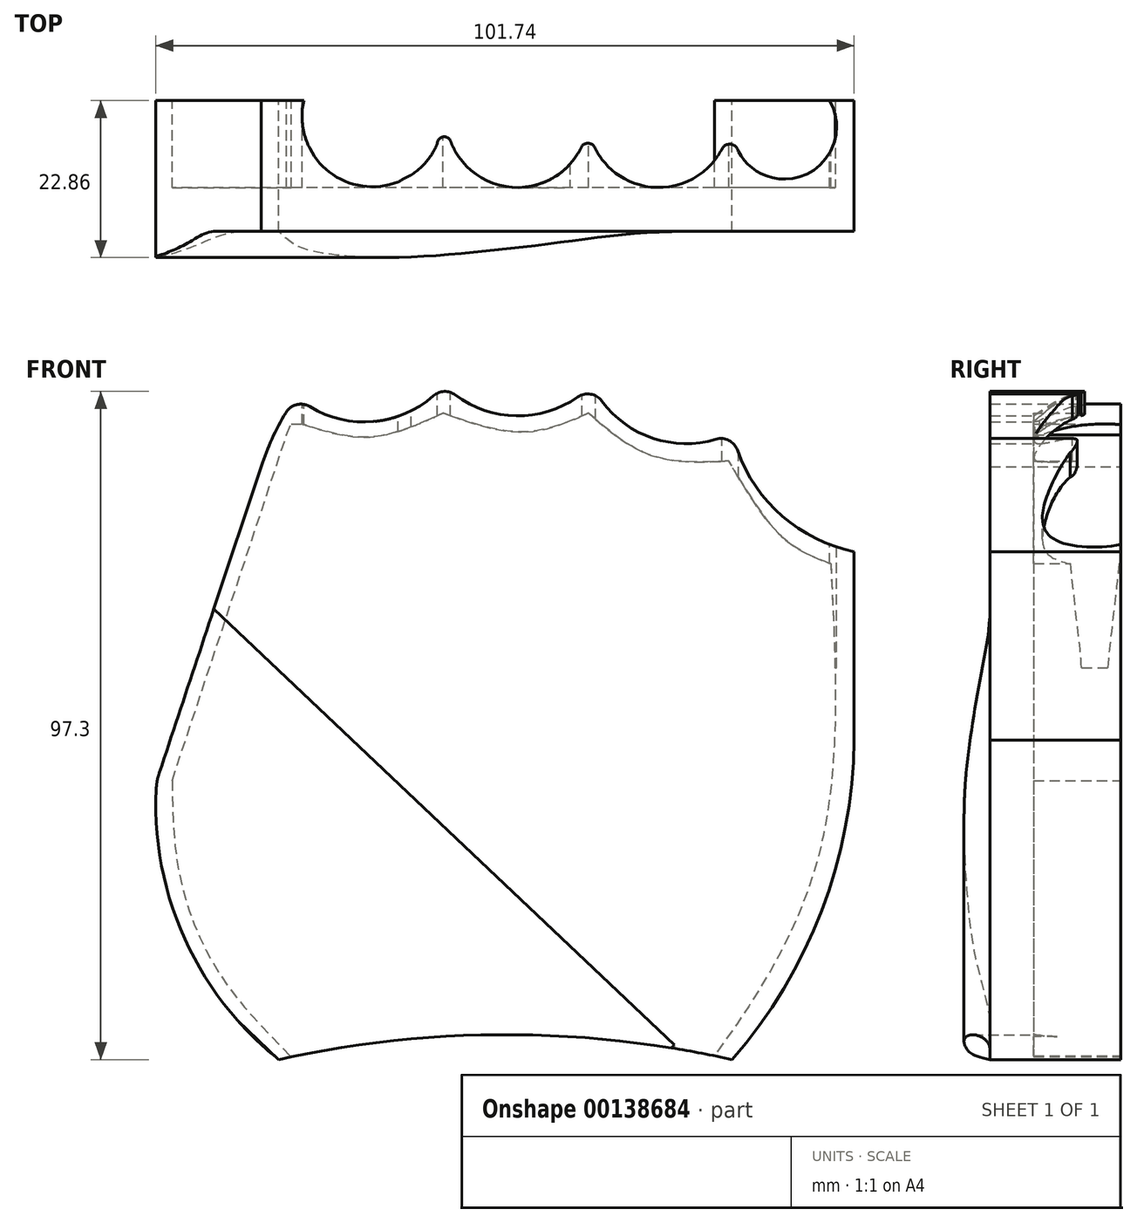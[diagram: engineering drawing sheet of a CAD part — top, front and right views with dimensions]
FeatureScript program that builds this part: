
annotation { "Feature Type Name" : "Feature", "Feature Type Description" : "" }
export const myFeature = defineFeature(function(context is Context, id is Id, definition is map)
    precondition{}
    {
        {
            var Q0;
            Q0=qCreatedBy(makeId("Front.planeOp"),FACE);
            var sketch = newSketch(context, id + "F0", { "sketchPlane" : qUnion([Q0])});
            skLineSegment(sketch, "E0", {"start": v(-118.33, 125.83) * mm, "end": v(-118.33, -51.97) * mm});
            skLineSegment(sketch, "E1", {"start": v(-118.33, -51.97) * mm, "end": v(59.47, -51.97) * mm});
            skPoint(sketch, "E2", {"position": v(-59.61, -44.35) * mm});
            skPoint(sketch, "E3", {"position": v(6.43, -44.35) * mm});
            skArc(sketch, "E4", {"start": v(6.43, -44.35) * mm, "mid": v(-26.6, -40.73) * mm, "end": v(-59.61, -44.35) * mm});
            skArc(sketch, "E5", {"start": v(6.43, -44.35) * mm, "mid": v(19.48, -22.66) * mm, "end": v(24.2, 2.2) * mm});
            skLineSegment(sketch, "E6", {"start": v(-77.4, -3.7) * mm, "end": v(47.54, -3.7) * mm});
            skArc(sketch, "E7", {"start": v(-77.47, -5) * mm, "mid": v(-73.3, -26.82) * mm, "end": v(-59.61, -44.35) * mm});
            skLineSegment(sketch, "E8", {"start": v(-77.03, -2.6) * mm, "end": v(-62.15, 42.01) * mm});
            skLineSegment(sketch, "E9", {"start": v(-57.07, 52.17) * mm, "end": v(-35.55, 53.88) * mm});
            skLineSegment(sketch, "E10", {"start": v(-35.55, 53.88) * mm, "end": v(-13.96, 53.88) * mm});
            skLineSegment(sketch, "E11", {"start": v(24.2, 2.2) * mm, "end": v(24.2, 29.63) * mm});
            skCircle(sketch, "E12", {"center": v(-21.51, -1.17) * mm, "radius": 22.35 * mm});
            skCircle(sketch, "E13", {"center": v(-21.51, -1.17) * mm, "radius": 15.75 * mm});
            skArc(sketch, "E14", {"start": v(-55.08, 50.73) * mm, "mid": v(-45.83, 48.57) * mm, "end": v(-37.1, 52.31) * mm});
            skArc(sketch, "E15", {"start": v(-33.9, 52.44) * mm, "mid": v(-25.02, 49.4) * mm, "end": v(-16.05, 52.13) * mm});
            skArc(sketch, "E16", {"start": v(24.2, 2.2) * mm, "mid": v(24.87, 15.91) * mm, "end": v(24.2, 29.63) * mm});
            skArc(sketch, "E17", {"start": v(-58.58, 49.87) * mm, "mid": v(-60.6, 46.05) * mm, "end": v(-62.15, 42.01) * mm});
            skLineSegment(sketch, "E18", {"start": v(-13.96, 53.88) * mm, "end": v(6.48, 46.93) * mm});
            skLineSegment(sketch, "E19", {"start": v(6.48, 46.93) * mm, "end": v(24.2, 29.63) * mm});
            skArc(sketch, "E20", {"start": v(-12.55, 51.55) * mm, "mid": v(-5.11, 46.14) * mm, "end": v(4.09, 45.99) * mm});
            skArc(sketch, "E21", {"start": v(7.21, 44.4) * mm, "mid": v(13.76, 34.78) * mm, "end": v(24.2, 29.63) * mm});
            skPoint(sketch, "E22.visualSharp", {"position": v(-62.15, 19.11) * mm});
            skPoint(sketch, "E23.visualSharp", {"position": v(-77.4, -3.7) * mm});
            skArc(sketch, "E23.filletArc", {"start": v(-77.03, -2.6) * mm, "mid": v(-77.33, -3.78) * mm, "end": v(-77.47, -5) * mm});
            skLineSegment(sketch, "E24.bottom", {"start": v(-118.33, 125.83) * mm, "end": v(-123.4, 125.83) * mm});
            skLineSegment(sketch, "E24.top", {"start": v(-118.33, -51.97) * mm, "end": v(-123.4, -51.97) * mm});
            skLineSegment(sketch, "E24.right", {"start": v(-123.4, 125.83) * mm, "end": v(-123.4, -51.97) * mm});
            skLineSegment(sketch, "E25.bottom", {"start": v(59.47, -51.97) * mm, "end": v(-123.4, -51.97) * mm});
            skLineSegment(sketch, "E25.top", {"start": v(59.47, -57.05) * mm, "end": v(-123.4, -57.05) * mm});
            skLineSegment(sketch, "E25.left", {"start": v(59.47, -51.97) * mm, "end": v(59.47, -57.05) * mm});
            skLineSegment(sketch, "E25.right", {"start": v(-123.4, -51.97) * mm, "end": v(-123.4, -57.05) * mm});
            skPoint(sketch, "E26.visualSharp", {"position": v(-57.07, 52.17) * mm});
            skArc(sketch, "E26.filletArc", {"start": v(-55.08, 50.73) * mm, "mid": v(-57, 51.03) * mm, "end": v(-58.58, 49.87) * mm});
            skPoint(sketch, "E27.visualSharp", {"position": v(-35.55, 53.88) * mm});
            skArc(sketch, "E27.filletArc", {"start": v(-33.9, 52.44) * mm, "mid": v(-35.51, 52.95) * mm, "end": v(-37.1, 52.31) * mm});
            skPoint(sketch, "E28.visualSharp", {"position": v(-13.96, 53.88) * mm});
            skArc(sketch, "E28.filletArc", {"start": v(-12.55, 51.55) * mm, "mid": v(-14.18, 52.55) * mm, "end": v(-16.05, 52.13) * mm});
            skPoint(sketch, "E29.visualSharp", {"position": v(6.48, 46.93) * mm});
            skArc(sketch, "E29.filletArc", {"start": v(7.21, 44.4) * mm, "mid": v(5.97, 45.82) * mm, "end": v(4.09, 45.99) * mm});
            skFitSpline(sketch, "E30", {"points": [v(-58.58, 49.87) * mm, v(-64.47, 22.99) * mm, v(-69.79, 19.11) * mm], "startDerivative": vector(-6.28, -49.5) * mm, "endDerivative": vector(-17.41, -7.17) * mm});
            skSolve(sketch);
        }
        {
            var Q0;
            {var subQ4=sQuery(id+"F0.wireOp",EDGE,"E11");Q0=makeQuery(id+"F0.imprint","IMPRINT",FACE,{"disambiguationData":[TD([[makeQuery(id+"F0.imprint","IMPRINT",EDGE,{"derivedFrom":subQ4}),1.0]])]});}
            var Q1;
            {var subQ7=sQuery(id+"F0.wireOp",EDGE,"E4");Q1=makeQuery(id+"F0.imprint","IMPRINT",FACE,{"disambiguationData":[TD([[makeQuery(id+"F0.imprint","IMPRINT",EDGE,{"derivedFrom":subQ7}),-1.0]])]});}
            var Q2;
            {var subQ0=sQuery(id+"F0.wireOp",EDGE,"E13");var subQ1=sQuery(id+"F0.wireOp",EDGE,"E6");var subQ2=makeQuery(id+"F0.imprint","INTERSECT",VERTEX,{"disambiguationData":[OD(0.0)],"derivedFrom":[subQ1,subQ0]});Q2=makeQuery(id+"F0.imprint","IMPRINT",FACE,{"disambiguationData":[TD([[makeQuery(id+"F0.imprint","IMPRINT",EDGE,{"disambiguationData":[TD([[subQ2,-1.0]])],"derivedFrom":subQ1}),1.0]])]});}
            var Q3;
            {var subQ4=sQuery(id+"F0.wireOp",EDGE,"E8");Q3=makeQuery(id+"F0.imprint","IMPRINT",FACE,{"disambiguationData":[TD([[makeQuery(id+"F0.imprint","IMPRINT",EDGE,{"derivedFrom":subQ4}),-1.0]])]});}
            var Q4;
            {var subQ0=sQuery(id+"F0.wireOp",EDGE,"E13");var subQ1=sQuery(id+"F0.wireOp",EDGE,"E6");var subQ2=makeQuery(id+"F0.imprint","INTERSECT",VERTEX,{"disambiguationData":[OD(0.0)],"derivedFrom":[subQ1,subQ0]});Q4=makeQuery(id+"F0.imprint","IMPRINT",FACE,{"disambiguationData":[TD([[makeQuery(id+"F0.imprint","IMPRINT",EDGE,{"disambiguationData":[TD([[subQ2,-1.0]])],"derivedFrom":subQ1}),-1.0]])]});}
            var Q5;
            {var subQ0=sQuery(id+"F0.wireOp",EDGE,"E12");var subQ1=sQuery(id+"F0.wireOp",EDGE,"E6");var subQ2=makeQuery(id+"F0.imprint","INTERSECT",VERTEX,{"disambiguationData":[OD(0.0)],"derivedFrom":[subQ1,subQ0]});Q5=makeQuery(id+"F0.imprint","IMPRINT",FACE,{"disambiguationData":[TD([[makeQuery(id+"F0.imprint","IMPRINT",EDGE,{"disambiguationData":[TD([[subQ2,-1.0]])],"derivedFrom":subQ1}),1.0]])]});}
            var Q6;
            {var subQ0=sQuery(id+"F0.wireOp",EDGE,"E12");var subQ1=sQuery(id+"F0.wireOp",EDGE,"E6");var subQ2=makeQuery(id+"F0.imprint","INTERSECT",VERTEX,{"disambiguationData":[OD(0.0)],"derivedFrom":[subQ1,subQ0]});Q6=makeQuery(id+"F0.imprint","IMPRINT",FACE,{"disambiguationData":[TD([[makeQuery(id+"F0.imprint","IMPRINT",EDGE,{"disambiguationData":[TD([[subQ2,-1.0]])],"derivedFrom":subQ1}),-1.0]])]});}
            extrude(context, id + "F1", {"entities" : qUnion([Q0, Q1, Q2, Q3, Q4, Q5, Q6]), "depth" : 13.97 * mm});
        }
        {
            var Q0;
            Q0=qCreatedBy(makeId("Top.planeOp"),FACE);
            cPlane(context, id + "F2", {"entities" : qUnion([Q0]), "cplaneType" : CPlaneType.OFFSET, "offset" : 63.5 * mm, "width" : 152.4 * mm, "height" : 152.4 * mm});
        }
        {
            var Q0;
            Q0=qCreatedBy(id+"F2.planeOp",FACE);
            var sketch = newSketch(context, id + "F3", { "sketchPlane" : qUnion([Q0])});
            skLineSegment(sketch, "E31.0.0", {"start": v(-77.47, 0) * mm, "end": v(-77.47, 0) * mm});
            skLineSegment(sketch, "E31.0.1", {"start": v(-77.47, 0) * mm, "end": v(-77.47, -13.97) * mm});
            skLineSegment(sketch, "E31.0.2", {"start": v(-77.47, -13.97) * mm, "end": v(-77.47, -13.97) * mm});
            skLineSegment(sketch, "E31.0.3", {"start": v(-77.47, 0) * mm, "end": v(-77.47, -13.97) * mm});
            skLineSegment(sketch, "E32.0", {"start": v(24.2, -13.97) * mm, "end": v(24.2, 0) * mm});
            skLineSegment(sketch, "E33.0", {"start": v(7.21, -13.97) * mm, "end": v(24.2, -13.97) * mm});
            skLineSegment(sketch, "E34.0", {"start": v(-12.55, -13.97) * mm, "end": v(4.09, -13.97) * mm});
            skCircle(sketch, "E35", {"center": v(14.05, -3.81) * mm, "radius": 7.62 * mm});
            skCircle(sketch, "E36", {"center": v(-4.27, -2.29) * mm, "radius": 10.37 * mm});
            skCircle(sketch, "E37", {"center": v(-45.97, -2.29) * mm, "radius": 10.26 * mm});
            skCircle(sketch, "E38", {"center": v(-24.86, -2.29) * mm, "radius": 10.37 * mm});
            skArc(sketch, "E39", {"start": v(-34.62, -5.8) * mm, "mid": v(-35.78, -5.3) * mm, "end": v(-36.53, -6.3) * mm});
            skArc(sketch, "E40", {"start": v(-13.46, -7.09) * mm, "mid": v(-14.28, -6.26) * mm, "end": v(-15.4, -6.55) * mm});
            skArc(sketch, "E41", {"start": v(7.33, -7.4) * mm, "mid": v(6.24, -6.35) * mm, "end": v(4.92, -7.08) * mm});
            skLineSegment(sketch, "E42", {"start": v(-36.2, 0.89) * mm, "end": v(-34.74, 0.89) * mm});
            skLineSegment(sketch, "E43", {"start": v(-15.1, 1.22) * mm, "end": v(-14.03, 1.22) * mm});
            skLineSegment(sketch, "E44", {"start": v(5.76, 0.32) * mm, "end": v(7.65, 0.32) * mm});
            skLineSegment(sketch, "E45", {"start": v(-39.1, -9.92) * mm, "end": v(-31.89, -9.92) * mm});
            skFitSpline(sketch, "E46", {"points": [v(-42.27, -11.86) * mm, v(-39.1, -10.37) * mm, v(-36.41, -9.92) * mm], "startDerivative": vector(6.02, 3.27) * mm, "endDerivative": vector(5.69, 0.55) * mm});
            skSolve(sketch);
        }
        {
            var Q0;
            {var subQ3=sQuery(id+"F3.wireOp",EDGE,"fkl0SDea-Ru4K-tGnn-LgRH-vELJiwKebO69");Q0=makeQuery(id+"F3.imprint","IMPRINT",FACE,{"disambiguationData":[TD([[makeQuery(id+"F3.imprint","IMPRINT",EDGE,{"derivedFrom":subQ3}),-1.0]])]});}
            var Q1;
            Q1=makeQuery(id+"F3.imprint","IMPRINT",FACE,{"disambiguationData":[TD([[makeQuery(id+"F3.imprint","IMPRINT",EDGE,{"derivedFrom":sQuery(id+"F3.wireOp",EDGE,"E38")}),1.0]])]});
            var Q2;
            Q2=makeQuery(id+"F3.imprint","IMPRINT",FACE,{"disambiguationData":[TD([[makeQuery(id+"F3.imprint","IMPRINT",EDGE,{"derivedFrom":sQuery(id+"F3.wireOp",EDGE,"E37")}),1.0]])]});
            var Q3;
            {var subQ0=sQuery(id+"F3.wireOp",EDGE,"E42");Q3=makeQuery(id+"F3.imprint","IMPRINT",FACE,{"disambiguationData":[TD([[makeQuery(id+"F3.imprint","IMPRINT",EDGE,{"derivedFrom":subQ0}),-1.0]])]});}
            var Q4;
            {var subQ0=sQuery(id+"F3.wireOp",EDGE,"E43");Q4=makeQuery(id+"F3.imprint","IMPRINT",FACE,{"disambiguationData":[TD([[makeQuery(id+"F3.imprint","IMPRINT",EDGE,{"derivedFrom":subQ0}),-1.0]])]});}
            var Q5;
            {var subQ0=sQuery(id+"F3.wireOp",EDGE,"E40");var subQ1=sQuery(id+"F3.wireOp",EDGE,"E36");var subQ2=makeQuery(id+"F3.imprint","INTERSECT",VERTEX,{"disambiguationData":[OD(1.0)],"derivedFrom":[subQ1,subQ0]});Q5=makeQuery(id+"F3.imprint","IMPRINT",FACE,{"disambiguationData":[TD([[makeQuery(id+"F3.imprint","IMPRINT",EDGE,{"disambiguationData":[TD([[subQ2,1.0]])],"derivedFrom":subQ1}),-1.0]])]});}
            var Q6;
            {var subQ0=sQuery(id+"F3.wireOp",EDGE,"E38");var subQ1=sQuery(id+"F3.wireOp",EDGE,"E36");var subQ2=makeQuery(id+"F3.imprint","INTERSECT",VERTEX,{"disambiguationData":[OD(0.0)],"derivedFrom":[subQ1,subQ0]});Q6=makeQuery(id+"F3.imprint","IMPRINT",FACE,{"disambiguationData":[TD([[makeQuery(id+"F3.imprint","IMPRINT",EDGE,{"disambiguationData":[TD([[subQ2,-1.0]])],"derivedFrom":subQ1}),1.0]])]});}
            extrude(context, id + "F4", {"entities" : qUnion([Q0, Q1, Q2, Q3, Q4, Q5, Q6]), "operationType" : NewBodyOperationType.REMOVE, "endBound" : BoundingType.THROUGH_ALL, "oppositeDirection" : true, "depth" : 134.62 * mm});
        }
        {
            var Q0;
            {var subQ0=sQuery(id+"F3.wireOp",EDGE,"E35");var subQ1=makeQuery(id+"F3.imprint","INTERSECT",VERTEX,{"derivedFrom":[subQ0,sQuery(id+"F3.wireOp",EDGE,"E44")]});Q0=makeQuery(id+"F3.imprint","IMPRINT",FACE,{"disambiguationData":[TD([[makeQuery(id+"F3.imprint","IMPRINT",EDGE,{"disambiguationData":[TD([[subQ1,-1.0]])],"derivedFrom":subQ0}),1.0]])]});}
            var Q1;
            {var subQ1=sQuery(id+"F3.wireOp",EDGE,"E36");var subQ7=makeQuery(id+"F3.imprint","INTERSECT",VERTEX,{"derivedFrom":[subQ1,sQuery(id+"F3.wireOp",EDGE,"E43")]});Q1=makeQuery(id+"F3.imprint","IMPRINT",FACE,{"disambiguationData":[TD([[makeQuery(id+"F3.imprint","IMPRINT",EDGE,{"disambiguationData":[TD([[subQ7,1.0]])],"derivedFrom":subQ1}),1.0]])]});}
            var Q2;
            {var subQ0=sQuery(id+"F3.wireOp",EDGE,"E44");Q2=makeQuery(id+"F3.imprint","IMPRINT",FACE,{"disambiguationData":[TD([[makeQuery(id+"F3.imprint","IMPRINT",EDGE,{"derivedFrom":subQ0}),-1.0]])]});}
            extrude(context, id + "F5", {"entities" : qUnion([Q0, Q1, Q2]), "operationType" : NewBodyOperationType.REMOVE, "oppositeDirection" : true, "depth" : 50.8 * mm});
        }
        {
            var Q0;
            Q0=qCreatedBy(makeId("Front.planeOp"),FACE);
            cPlane(context, id + "F6", {"entities" : qUnion([Q0]), "cplaneType" : CPlaneType.OFFSET, "offset" : 25.4 * mm, "oppositeDirection" : true, "width" : 152.4 * mm, "height" : 152.4 * mm});
        }
        {
            var Q0;
            Q0=qCreatedBy(id+"F6.planeOp",FACE);
            var sketch = newSketch(context, id + "F7", { "sketchPlane" : qUnion([Q0])});
            skLineSegment(sketch, "E47.0", {"start": v(24.2, 2.2) * mm, "end": v(24.2, 29.63) * mm});
            skArc(sketch, "E47.1", {"start": v(6.43, -44.35) * mm, "mid": v(19.48, -22.66) * mm, "end": v(24.2, 2.2) * mm});
            skLineSegment(sketch, "E47.2", {"start": v(-77.03, -2.6) * mm, "end": v(-62.15, 42.01) * mm});
            skArc(sketch, "E47.3", {"start": v(-77.47, -5) * mm, "mid": v(-73.3, -26.82) * mm, "end": v(-59.61, -44.35) * mm});
            skArc(sketch, "E47.4", {"start": v(-77.03, -2.6) * mm, "mid": v(-77.33, -3.78) * mm, "end": v(-77.47, -5) * mm});
            skArc(sketch, "E48.0", {"start": v(20.65, 30.66) * mm, "mid": v(22.4, 30.07) * mm, "end": v(24.2, 29.63) * mm});
            skArc(sketch, "E49.0", {"start": v(7.21, 44.4) * mm, "mid": v(13.76, 34.78) * mm, "end": v(24.2, 29.63) * mm});
            skArc(sketch, "E50.0", {"start": v(-58.58, 49.87) * mm, "mid": v(-60.6, 46.05) * mm, "end": v(-62.15, 42.01) * mm});
            skArc(sketch, "E51.0", {"start": v(6.43, -44.35) * mm, "mid": v(-3.92, -42.42) * mm, "end": v(-14.38, -41.21) * mm});
            skArc(sketch, "E52.0", {"start": v(-55.97, -43.58) * mm, "mid": v(-49.14, -42.4) * mm, "end": v(-42.27, -41.53) * mm});
            skArc(sketch, "E53.0", {"start": v(-55.97, -43.58) * mm, "mid": v(-57.8, -43.95) * mm, "end": v(-59.61, -44.35) * mm});
            skFitSpline(sketch, "E54", {"points": [v(20.65, 30.66) * mm, v(18.83, -15.4) * mm, v(3.84, -43.8) * mm], "startDerivative": vector(5.6, -101.34) * mm, "endDerivative": vector(-40.72, -55.26) * mm});
            skFitSpline(sketch, "E55", {"points": [v(20.66, 27.9) * mm, v(13.98, 31.53) * mm, v(5.95, 42.8) * mm], "startDerivative": vector(-16.07, 6.16) * mm, "endDerivative": vector(-13.47, 22.81) * mm});
            skFitSpline(sketch, "E56", {"points": [v(5.95, 42.8) * mm, v(-5.4, 43.66) * mm, v(-14.49, 49.79) * mm], "startDerivative": vector(-23.56, -1) * mm, "endDerivative": vector(-17.3, 15.02) * mm});
            skFitSpline(sketch, "E57", {"points": [v(-14.49, 49.79) * mm, v(-23.94, 47.05) * mm, v(-35.67, 49.79) * mm], "startDerivative": vector(-19.34, -8.38) * mm, "endDerivative": vector(-22.97, 8.1) * mm});
            skFitSpline(sketch, "E58", {"points": [v(-35.67, 49.79) * mm, v(-46.36, 46.32) * mm, v(-56.2, 48.2) * mm], "startDerivative": vector(-20.9, -9.5) * mm, "endDerivative": vector(-20.15, 6.46) * mm});
            skLineSegment(sketch, "E59", {"start": v(-56.2, 48.2) * mm, "end": v(-57.8, 48.2) * mm});
            skLineSegment(sketch, "E60", {"start": v(-57.8, 48.2) * mm, "end": v(-58.47, 46.62) * mm});
            skLineSegment(sketch, "E61", {"start": v(-58.47, 46.62) * mm, "end": v(-75.15, -3.72) * mm});
            skFitSpline(sketch, "E62", {"points": [v(-75.15, -3.72) * mm, v(-74, -17.79) * mm, v(-68, -32.23) * mm, v(-57.8, -43.95) * mm], "startDerivative": vector(0.7, -43.46) * mm, "endDerivative": vector(32.47, -33.02) * mm});
            skArc(sketch, "E63.0", {"start": v(6.43, -44.35) * mm, "mid": v(-26.6, -40.73) * mm, "end": v(-59.61, -44.35) * mm});
            skFitSpline(sketch, "E64", {"points": [v(3.84, -43.8) * mm, v(-24.07, -40.75) * mm, v(-57.8, -43.95) * mm], "startDerivative": vector(-59.57, 9.54) * mm, "endDerivative": vector(-65.83, -9.19) * mm});
            skLineSegment(sketch, "E65", {"start": v(20.66, 27.9) * mm, "end": v(20.8, 27.9) * mm});
            skLineSegment(sketch, "E66", {"start": v(20.8, 27.9) * mm, "end": v(20.8, 27.89) * mm});
            skLineSegment(sketch, "E67", {"start": v(3.84, -43.8) * mm, "end": v(-57.8, -43.95) * mm});
            skSolve(sketch);
        }
        {
            var Q0;
            {var subQ4=sQuery(id+"F7.wireOp",EDGE,"E67");Q0=makeQuery(id+"F7.imprint","IMPRINT",FACE,{"disambiguationData":[TD([[makeQuery(id+"F7.imprint","IMPRINT",EDGE,{"derivedFrom":subQ4}),-1.0]])]});}
            var Q1;
            Q1=makeQuery(id+"F7.imprint","IMPRINT",FACE,{"disambiguationData":[TD([[makeQuery(id+"F7.imprint","IMPRINT",EDGE,{"derivedFrom":sQuery(id+"F7.wireOp",EDGE,"E55")}),1.0]])]});
            extrude(context, id + "F8", {"entities" : qUnion([Q0, Q1]), "operationType" : NewBodyOperationType.REMOVE, "depth" : 38.1 * mm});
        }
        {
            var Q0;
            Q0=makeQuery(id+"F1.opExtrude","SWEPT_EDGE",EDGE,{"disambiguationData":[OSD([sQuery(id+"F0.wireOp",EDGE,"E8"),sQuery(id+"F0.wireOp",EDGE,"E17")])]});
            var Q1;
            Q1=makeQuery(id+"F1.opExtrude","SWEPT_EDGE",EDGE,{"disambiguationData":[OSD([sQuery(id+"F0.wireOp",EDGE,"E8"),sQuery(id+"F0.wireOp",EDGE,"E23.filletArc")])]});
            cPlane(context, id + "F9", {"entities" : qUnion([Q0, Q1]), "cplaneType" : CPlaneType.LINE_ANGLE, "offset" : 25.4 * mm, "angle" : 25 * degree, "width" : 152.4 * mm, "height" : 152.4 * mm});
        }
        {
            var Q0;
            Q0=qCreatedBy(id+"F9.planeOp",FACE);
            var sketch = newSketch(context, id + "F10", { "sketchPlane" : qUnion([Q0])});
            skLineSegment(sketch, "E68.0.0", {"start": v(0, -12.22) * mm, "end": v(0, -54.85) * mm});
            skLineSegment(sketch, "E68.0.1", {"start": v(0, -54.85) * mm, "end": v(13.97, -54.85) * mm});
            skLineSegment(sketch, "E68.0.2", {"start": v(13.97, -54.85) * mm, "end": v(13.97, -12.22) * mm});
            skLineSegment(sketch, "E68.0.3", {"start": v(13.97, -12.22) * mm, "end": v(0, -12.22) * mm});
            skLineSegment(sketch, "E69.0.0", {"start": v(0, -56.89) * mm, "end": v(0, -73.37) * mm});
            skLineSegment(sketch, "E69.0.1", {"start": v(0, -73.19) * mm, "end": v(13.97, -73.19) * mm});
            skLineSegment(sketch, "E69.0.2", {"start": v(13.97, -73.37) * mm, "end": v(13.97, -56.89) * mm});
            skLineSegment(sketch, "E69.0.3", {"start": v(13.97, -56.89) * mm, "end": v(0, -56.89) * mm});
            skLineSegment(sketch, "E70.0.0", {"start": v(0, -54.85) * mm, "end": v(0, -56.89) * mm});
            skLineSegment(sketch, "E70.0.1", {"start": v(0, -56.89) * mm, "end": v(13.97, -56.89) * mm});
            skLineSegment(sketch, "E70.0.2", {"start": v(13.97, -56.89) * mm, "end": v(13.97, -54.85) * mm});
            skLineSegment(sketch, "E70.0.3", {"start": v(13.97, -54.85) * mm, "end": v(0, -54.85) * mm});
            skLineSegment(sketch, "E71.bottom", {"start": v(13.97, -12.22) * mm, "end": v(19.05, -12.22) * mm});
            skLineSegment(sketch, "E71.top", {"start": v(13.97, -73.19) * mm, "end": v(19.05, -73.19) * mm});
            skLineSegment(sketch, "E71.left", {"start": v(13.97, -12.22) * mm, "end": v(13.97, -73.19) * mm});
            skLineSegment(sketch, "E71.right", {"start": v(19.05, -12.22) * mm, "end": v(19.05, -73.19) * mm});
            skFitSpline(sketch, "E72", {"points": [v(19.05, -32.04) * mm, v(20.74, -42.94) * mm, v(22.1, -51.28) * mm, v(22.86, -60.24) * mm, v(21.84, -69.41) * mm, v(19.05, -73.19) * mm], "startDerivative": vector(1.3, -50.2) * mm, "endDerivative": vector(-32.1, -26.15) * mm});
            skFitSpline(sketch, "E73", {"points": [v(9.43, -42.23) * mm, v(15.53, -51.96) * mm, v(17.18, -60.38) * mm, v(10.58, -67.06) * mm, v(0, -66.8) * mm], "startDerivative": vector(24.91, -36.13) * mm, "endDerivative": vector(-42.63, 8.16) * mm});
            skFitSpline(sketch, "E74", {"points": [v(0, -41.9) * mm, v(5.72, -40.67) * mm, v(9.43, -42.23) * mm], "startDerivative": vector(11.08, 3.83) * mm, "endDerivative": vector(7.67, -4.75) * mm});
            skSolve(sketch);
        }
        {
            var Q0;
            Q0=qCreatedBy(makeId("Front.planeOp"),FACE);
            cPlane(context, id + "F11", {"entities" : qUnion([Q0]), "cplaneType" : CPlaneType.OFFSET, "offset" : 25.4 * mm, "width" : 152.4 * mm, "height" : 152.4 * mm});
        }
        {
            var Q0;
            Q0=makeQuery(id+"F1.opExtrude","CAP_FACE",FACE,{"disambiguationData":[OSD([sQuery(id+"F0.wireOp",EDGE,"E4"),sQuery(id+"F0.wireOp",EDGE,"E5"),sQuery(id+"F0.wireOp",EDGE,"E7"),sQuery(id+"F0.wireOp",EDGE,"E8"),sQuery(id+"F0.wireOp",EDGE,"E11"),sQuery(id+"F0.wireOp",EDGE,"E14"),sQuery(id+"F0.wireOp",EDGE,"E15"),sQuery(id+"F0.wireOp",EDGE,"E17"),sQuery(id+"F0.wireOp",EDGE,"E20"),sQuery(id+"F0.wireOp",EDGE,"E21"),sQuery(id+"F0.wireOp",EDGE,"E23.filletArc"),sQuery(id+"F0.wireOp",EDGE,"E26.filletArc"),sQuery(id+"F0.wireOp",EDGE,"E27.filletArc"),sQuery(id+"F0.wireOp",EDGE,"E28.filletArc"),sQuery(id+"F0.wireOp",EDGE,"E29.filletArc")])],"isStart":false});
            extrude(context, id + "F12", {"entities" : qUnion([Q0]), "operationType" : NewBodyOperationType.ADD, "depth" : 5.08 * mm});
        }
        {
            var Q0;
            {var subQ0=sQuery(id+"F10.wireOp",EDGE,"E72");Q0=makeQuery(id+"F10.imprint","IMPRINT",FACE,{"disambiguationData":[TD([[makeQuery(id+"F10.imprint","IMPRINT",EDGE,{"derivedFrom":subQ0}),-1.0]])]});}
            extrude(context, id + "F13", {"entities" : qUnion([Q0]), "operationType" : NewBodyOperationType.ADD, "oppositeDirection" : true, "depth" : 101.6 * mm});
        }
        {
            var Q0;
            {var subQ1=sQuery(id+"F0.wireOp",EDGE,"E8");var subQ4=sQuery(id+"F10.wireOp",EDGE,"E71.right");Q0=makeQuery(id+"F13.boolean.opBoolean","SPLIT",FACE,{"disambiguationData":[TD([makeQuery(id+"F1.opExtrude","SWEPT_FACE",FACE,{"disambiguationData":[OSD([subQ1])]})])],"derivedFrom":makeQuery(id+"F13.opExtrude","SWEPT_FACE",FACE,{"disambiguationData":[OSD([subQ4])]})});}
            var Q1;
            {var subQ1=sQuery(id+"F0.wireOp",EDGE,"E4");var subQ3=sQuery(id+"F10.wireOp",EDGE,"E71.right");Q1=makeQuery(id+"F13.boolean.opBoolean","SPLIT",FACE,{"disambiguationData":[TD([makeQuery(id+"F1.opExtrude","SWEPT_FACE",FACE,{"disambiguationData":[OSD([subQ1])]})])],"derivedFrom":makeQuery(id+"F13.opExtrude","SWEPT_FACE",FACE,{"disambiguationData":[OSD([subQ3])]})});}
            extrude(context, id + "F14", {"entities" : qUnion([Q0, Q1]), "operationType" : NewBodyOperationType.REMOVE, "oppositeDirection" : true, "depth" : 25.4 * mm});
        }
        {
            var Q0;
            Q0=qCreatedBy(id+"F9.planeOp",FACE);
            cPlane(context, id + "F15", {"entities" : qUnion([Q0]), "cplaneType" : CPlaneType.OFFSET, "offset" : 101.6 * mm, "oppositeDirection" : true, "width" : 152.4 * mm, "height" : 152.4 * mm});
        }
        {
            var Q0;
            Q0=qCreatedBy(id+"F9.planeOp",FACE);
            cPlane(context, id + "F16", {"entities" : qUnion([Q0]), "cplaneType" : CPlaneType.OFFSET, "offset" : 50.8 * mm, "oppositeDirection" : true, "width" : 152.4 * mm, "height" : 152.4 * mm});
        }
        {
            var Q0;
            Q0=qCreatedBy(id+"F11.planeOp",FACE);
            cPlane(context, id + "F17", {"entities" : qUnion([Q0]), "cplaneType" : CPlaneType.OFFSET, "offset" : 25.4 * mm, "oppositeDirection" : true, "width" : 152.4 * mm, "height" : 152.4 * mm});
        }
    });
